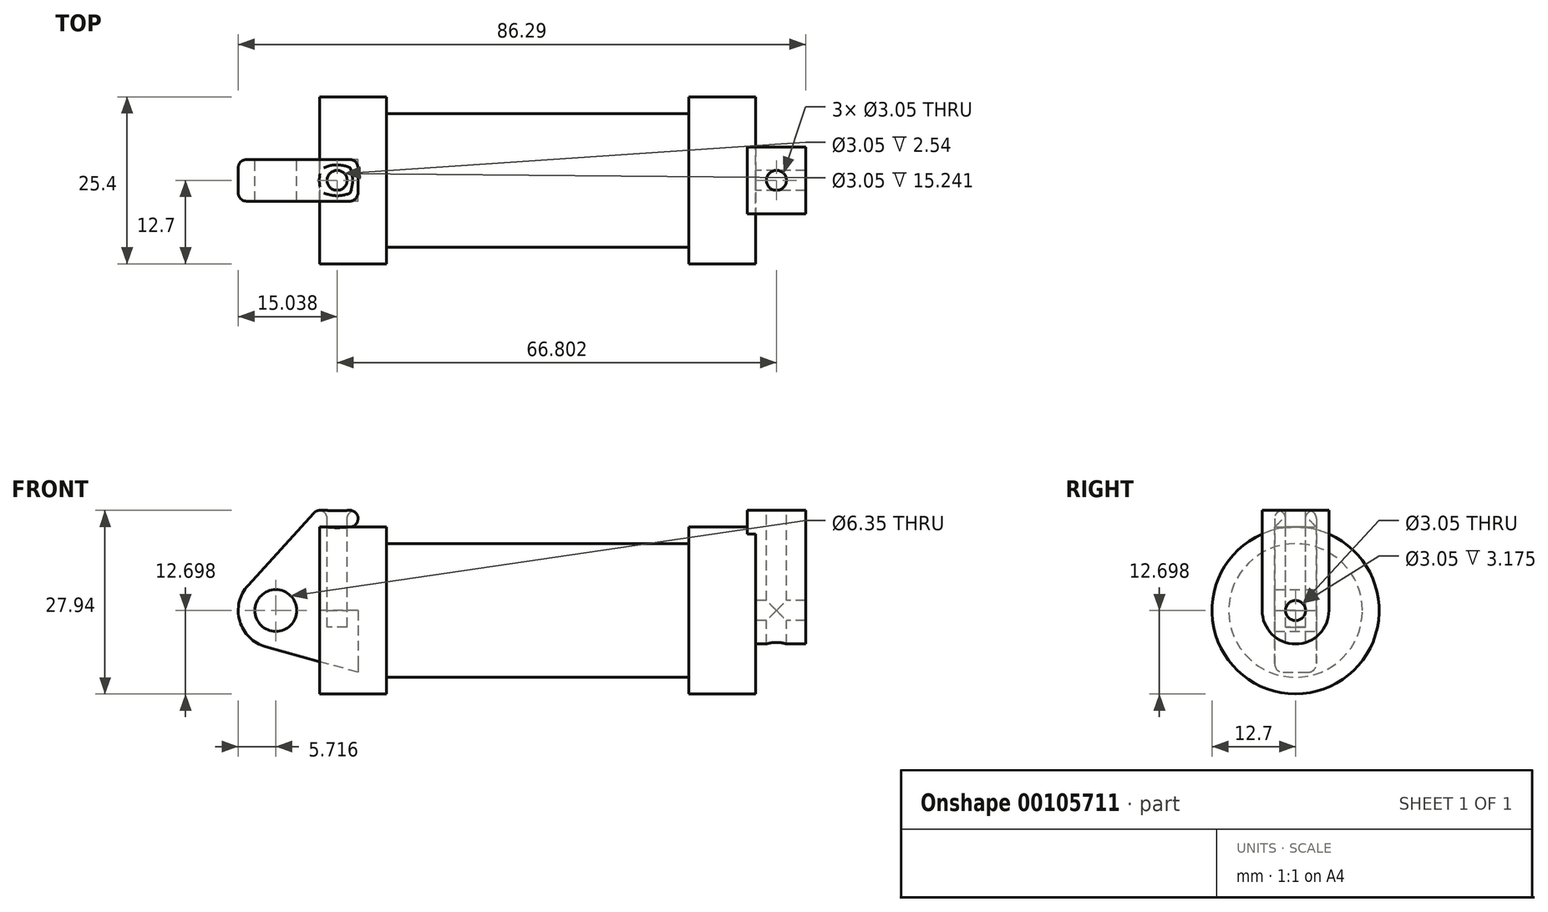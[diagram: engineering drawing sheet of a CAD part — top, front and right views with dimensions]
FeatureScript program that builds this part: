
annotation { "Feature Type Name" : "Feature", "Feature Type Description" : "" }
export const myFeature = defineFeature(function(context is Context, id is Id, definition is map)
    precondition{}
    {
        {
            var Q0;
            Q0=qCreatedBy(makeId("Front.planeOp"),FACE);
            var sketch = newSketch(context, id + "F0", { "sketchPlane" : qUnion([Q0])});
            skLineSegment(sketch, "E0", {"start": v(-16.68, -6.1) * mm, "end": v(-16.68, 6.6) * mm});
            skLineSegment(sketch, "E1", {"start": v(-16.68, 6.6) * mm, "end": v(-6.52, 6.6) * mm});
            skLineSegment(sketch, "E2", {"start": v(-6.52, 6.6) * mm, "end": v(-6.52, 4.07) * mm});
            skLineSegment(sketch, "E3", {"start": v(-6.52, 4.07) * mm, "end": v(39.46, 4.07) * mm});
            skLineSegment(sketch, "E4", {"start": v(39.46, 4.07) * mm, "end": v(39.46, 6.6) * mm});
            skLineSegment(sketch, "E5", {"start": v(39.46, 6.6) * mm, "end": v(49.62, 6.6) * mm});
            skLineSegment(sketch, "E6", {"start": v(49.62, 6.6) * mm, "end": v(49.62, -6.1) * mm});
            skLineSegment(sketch, "E7", {"start": v(49.62, -6.1) * mm, "end": v(-16.68, -6.1) * mm});
            skLineSegment(sketch, "E8", {"start": v(-10.84, 9.15) * mm, "end": v(-17.19, 9.15) * mm});
            skLineSegment(sketch, "E9", {"start": v(-17.19, 9.15) * mm, "end": v(-27.56, -2.24) * mm});
            skLineSegment(sketch, "E10", {"start": v(-16.68, -6.1) * mm, "end": v(-23.33, -6.1) * mm});
            skCircle(sketch, "E11", {"center": v(-23.33, -6.1) * mm, "radius": 5.72 * mm});
            skCircle(sketch, "E12", {"center": v(-23.33, -6.1) * mm, "radius": 3.18 * mm});
            skLineSegment(sketch, "E13", {"start": v(-10.84, 9.15) * mm, "end": v(-10.84, -15.49) * mm});
            skLineSegment(sketch, "E14", {"start": v(-10.84, -15.49) * mm, "end": v(-24.86, -11.6) * mm});
            skSolve(sketch);
        }
        {
            var Q0;
            {var subQ0=sQuery(id+"F0.wireOp",EDGE,"E2");Q0=makeQuery(id+"F0.imprint","IMPRINT",FACE,{"disambiguationData":[TD([[makeQuery(id+"F0.imprint","IMPRINT",EDGE,{"derivedFrom":subQ0}),-1.0]])]});}
            var Q1;
            {var subQ0=sQuery(id+"F0.wireOp",EDGE,"E0");Q1=makeQuery(id+"F0.imprint","IMPRINT",FACE,{"disambiguationData":[TD([[makeQuery(id+"F0.imprint","IMPRINT",EDGE,{"derivedFrom":subQ0}),-1.0]])]});}
            var Q2;
            Q2=sQuery(id+"F0.wireOp",EDGE,"E7");
            revolve(context, id + "F1", {"entities" : qUnion([Q0, Q1]), "axis" : qUnion([Q2]), "revolveType" : RevolveType.FULL});
        }
        {
            var Q0;
            {var subQ3=sQuery(id+"F0.wireOp",EDGE,"E0");Q0=makeQuery(id+"F0.imprint","IMPRINT",FACE,{"disambiguationData":[TD([[makeQuery(id+"F0.imprint","IMPRINT",EDGE,{"derivedFrom":subQ3}),1.0]])]});}
            var Q1;
            {var subQ4=sQuery(id+"F0.wireOp",EDGE,"E12");Q1=makeQuery(id+"F0.imprint","IMPRINT",FACE,{"disambiguationData":[TD([[makeQuery(id+"F0.imprint","IMPRINT",EDGE,{"derivedFrom":subQ4}),-1.0]])]});}
            var Q2;
            {var subQ0=sQuery(id+"F0.wireOp",EDGE,"E14");Q2=makeQuery(id+"F0.imprint","IMPRINT",FACE,{"disambiguationData":[TD([[makeQuery(id+"F0.imprint","IMPRINT",EDGE,{"derivedFrom":subQ0}),-1.0]])]});}
            extrude(context, id + "F2", {"entities" : qUnion([Q0, Q1, Q2]), "endBound" : BoundingType.SYMMETRIC, "depth" : 6.35 * mm});
        }
        {
            var Q0;
            Q0=makeQuery(id+"F1.opRevolve","SWEPT_FACE",FACE,{"disambiguationData":[OSD([sQuery(id+"F0.wireOp",EDGE,"E6")])]});
            var sketch = newSketch(context, id + "F3", { "sketchPlane" : qUnion([Q0])});
            skCircle(sketch, "E15", {"center": v(0, -6.1) * mm, "radius": 5.08 * mm});
            skCircle(sketch, "E16", {"center": v(0, -6.1) * mm, "radius": 1.52 * mm});
            skLineSegment(sketch, "E17", {"start": v(-5.08, -6.1) * mm, "end": v(-5.08, 9.15) * mm});
            skLineSegment(sketch, "E18", {"start": v(-5.08, 9.15) * mm, "end": v(5.08, 9.15) * mm});
            skLineSegment(sketch, "E19", {"start": v(5.08, 9.15) * mm, "end": v(5.08, -6.1) * mm});
            skSolve(sketch);
        }
        {
            var Q0;
            Q0=makeQuery(id+"F3.imprint","IMPRINT",FACE,{"disambiguationData":[TD([[makeQuery(id+"F3.imprint","IMPRINT",EDGE,{"derivedFrom":sQuery(id+"F3.wireOp",EDGE,"E16")}),-1.0]])]});
            var Q1;
            {var subQ0=sQuery(id+"F3.wireOp",EDGE,"E18");Q1=makeQuery(id+"F3.imprint","IMPRINT",FACE,{"disambiguationData":[TD([[makeQuery(id+"F3.imprint","IMPRINT",EDGE,{"derivedFrom":subQ0}),-1.0]])]});}
            var Q2;
            {var subQ0=sQuery(id+"F3.wireOp",EDGE,"E17");var subQ1=sQuery(id+"F3.wireOp",EDGE,"E15");var subQ2=makeQuery(id+"F3.imprint","INTERSECT",VERTEX,{"derivedFrom":[subQ1,subQ0]});Q2=makeQuery(id+"F3.imprint","IMPRINT",FACE,{"disambiguationData":[TD([[makeQuery(id+"F3.imprint","IMPRINT",EDGE,{"disambiguationData":[TD([[subQ2,1.0]])],"derivedFrom":subQ1}),-1.0]])]});}
            extrude(context, id + "F4", {"entities" : qUnion([Q0, Q1, Q2]), "operationType" : NewBodyOperationType.ADD, "depth" : 7.62 * mm, "hasSecondDirection" : true, "secondDirectionOppositeDirection" : true, "secondDirectionDepth" : 1.27 * mm});
        }
        {
            var Q0;
            Q0=makeQuery(id+"F2.opExtrude","SWEPT_FACE",FACE,{"disambiguationData":[OSD([sQuery(id+"F0.wireOp",EDGE,"E8")])]});
            var sketch = newSketch(context, id + "F5", { "sketchPlane" : qUnion([Q0])});
            skCircle(sketch, "E20", {"center": v(-14.01, 0) * mm, "radius": 1.52 * mm});
            skPoint(sketch, "E20.centerSnap0", {"position": v(-14.01, 3.18) * mm});
            skPoint(sketch, "E20.centerSnap1", {"position": v(-17.19, 0) * mm});
            skSolve(sketch);
        }
        {
            var Q0;
            Q0=makeQuery(id+"F5.imprint","IMPRINT",FACE,{"disambiguationData":[TD([[makeQuery(id+"F5.imprint","IMPRINT",EDGE,{"derivedFrom":sQuery(id+"F5.wireOp",EDGE,"E20")}),1.0]])]});
            extrude(context, id + "F6", {"entities" : qUnion([Q0]), "operationType" : NewBodyOperationType.REMOVE, "oppositeDirection" : true, "depth" : 17.78 * mm});
        }
        {
            var Q0;
            Q0=makeQuery(id+"F4.opExtrude","SWEPT_FACE",FACE,{"disambiguationData":[OSD([sQuery(id+"F3.wireOp",EDGE,"E18")])]});
            var sketch = newSketch(context, id + "F7", { "sketchPlane" : qUnion([Q0])});
            skCircle(sketch, "E21", {"center": v(52.8, 0) * mm, "radius": 1.52 * mm});
            skPoint(sketch, "E21.centerSnap0", {"position": v(57.24, 0) * mm});
            skPoint(sketch, "E21.centerSnap1", {"position": v(52.8, -5.08) * mm});
            skSolve(sketch);
        }
        {
            var Q0;
            Q0 = qSketchRegion(id + "F7", true);
            extrude(context, id + "F8", {"entities" : qUnion([Q0]), "operationType" : NewBodyOperationType.REMOVE, "oppositeDirection" : true, "depth" : 25.4 * mm});
        }
        {
            var Q0;
            Q0=makeQuery(id+"F1.opRevolve","SWEPT_FACE",FACE,{"disambiguationData":[OSD([sQuery(id+"F0.wireOp",EDGE,"E4")])]});
            var Q1;
            Q1=makeQuery(id+"F4.boolean.opBoolean","INTERSECT",EDGE,{"derivedFrom":[makeQuery(id+"F1.opRevolve","SWEPT_FACE",FACE,{"disambiguationData":[OSD([sQuery(id+"F0.wireOp",EDGE,"E5")])]}),makeQuery(id+"F4.opExtrude","CAP_FACE",FACE,{"disambiguationData":[OSD([sQuery(id+"F3.wireOp",EDGE,"E15"),sQuery(id+"F3.wireOp",EDGE,"E16"),sQuery(id+"F3.wireOp",EDGE,"E17"),sQuery(id+"F3.wireOp",EDGE,"E18"),sQuery(id+"F3.wireOp",EDGE,"E19")])],"isStart":true})]});
            var Q2;
            Q2=makeQuery(id+"F4.opExtrude","CAP_FACE",FACE,{"disambiguationData":[OSD([sQuery(id+"F3.wireOp",EDGE,"E15"),sQuery(id+"F3.wireOp",EDGE,"E16"),sQuery(id+"F3.wireOp",EDGE,"E17"),sQuery(id+"F3.wireOp",EDGE,"E18"),sQuery(id+"F3.wireOp",EDGE,"E19")])],"isStart":true});
            var Q3;
            Q3=makeQuery(id+"F4.opExtrude","SWEPT_FACE",FACE,{"disambiguationData":[OSD([sQuery(id+"F3.wireOp",EDGE,"E18")])]});
            var Q4;
            Q4=makeQuery(id+"F4.opExtrude","CAP_FACE",FACE,{"disambiguationData":[OSD([sQuery(id+"F3.wireOp",EDGE,"E15"),sQuery(id+"F3.wireOp",EDGE,"E16"),sQuery(id+"F3.wireOp",EDGE,"E17"),sQuery(id+"F3.wireOp",EDGE,"E18"),sQuery(id+"F3.wireOp",EDGE,"E19")])],"isStart":false});
            var Q5;
            Q5=makeQuery(id+"F4.boolean.opBoolean","SPLIT",FACE,{"disambiguationData":[TD([makeQuery(id+"F1.opRevolve","SWEPT_FACE",FACE,{"disambiguationData":[OSD([sQuery(id+"F0.wireOp",EDGE,"E5")])]})])],"derivedFrom":makeQuery(id+"F1.opRevolve","SWEPT_FACE",FACE,{"disambiguationData":[OSD([sQuery(id+"F0.wireOp",EDGE,"E6")])]})});
            var Q6;
            Q6=makeQuery(id+"F1.opRevolve","SWEPT_FACE",FACE,{"disambiguationData":[OSD([sQuery(id+"F0.wireOp",EDGE,"E1")])]});
            var Q7;
            Q7=makeQuery(id+"F1.opRevolve","SWEPT_FACE",FACE,{"disambiguationData":[OSD([sQuery(id+"F0.wireOp",EDGE,"E2")])]});
            var Q8;
            {var subQ0=sQuery(id+"F0.wireOp",EDGE,"E13");Q8=makeQuery(id+"F2.opExtrude","SWEPT_FACE",FACE,{"disambiguationData":[OSD([subQ0]),TDD([makeQuery(id+"F0.imprint","IMPRINT",EDGE,{"disambiguationData":[TD([[makeQuery(id+"F0.imprint","INTERSECT",VERTEX,{"derivedFrom":[sQuery(id+"F0.wireOp",EDGE,"E8"),subQ0]}),-1.0]])],"derivedFrom":subQ0})])]});}
            var Q9;
            Q9=makeQuery(id+"F2.opExtrude","SWEPT_FACE",FACE,{"disambiguationData":[OSD([sQuery(id+"F0.wireOp",EDGE,"E8")])]});
            var Q10;
            Q10=makeQuery(id+"F2.opExtrude","SWEPT_FACE",FACE,{"disambiguationData":[OSD([sQuery(id+"F0.wireOp",EDGE,"E9")])]});
            fillet(context, id + "F9", {"entities" : qUnion([Q0, Q1, Q2, Q3, Q4, Q5, Q6, Q7, Q8, Q9, Q10]), "radius" : 1.27 * mm, "tangentPropagation" : true, "allowEdgeOverflow" : false});
        }
    });
